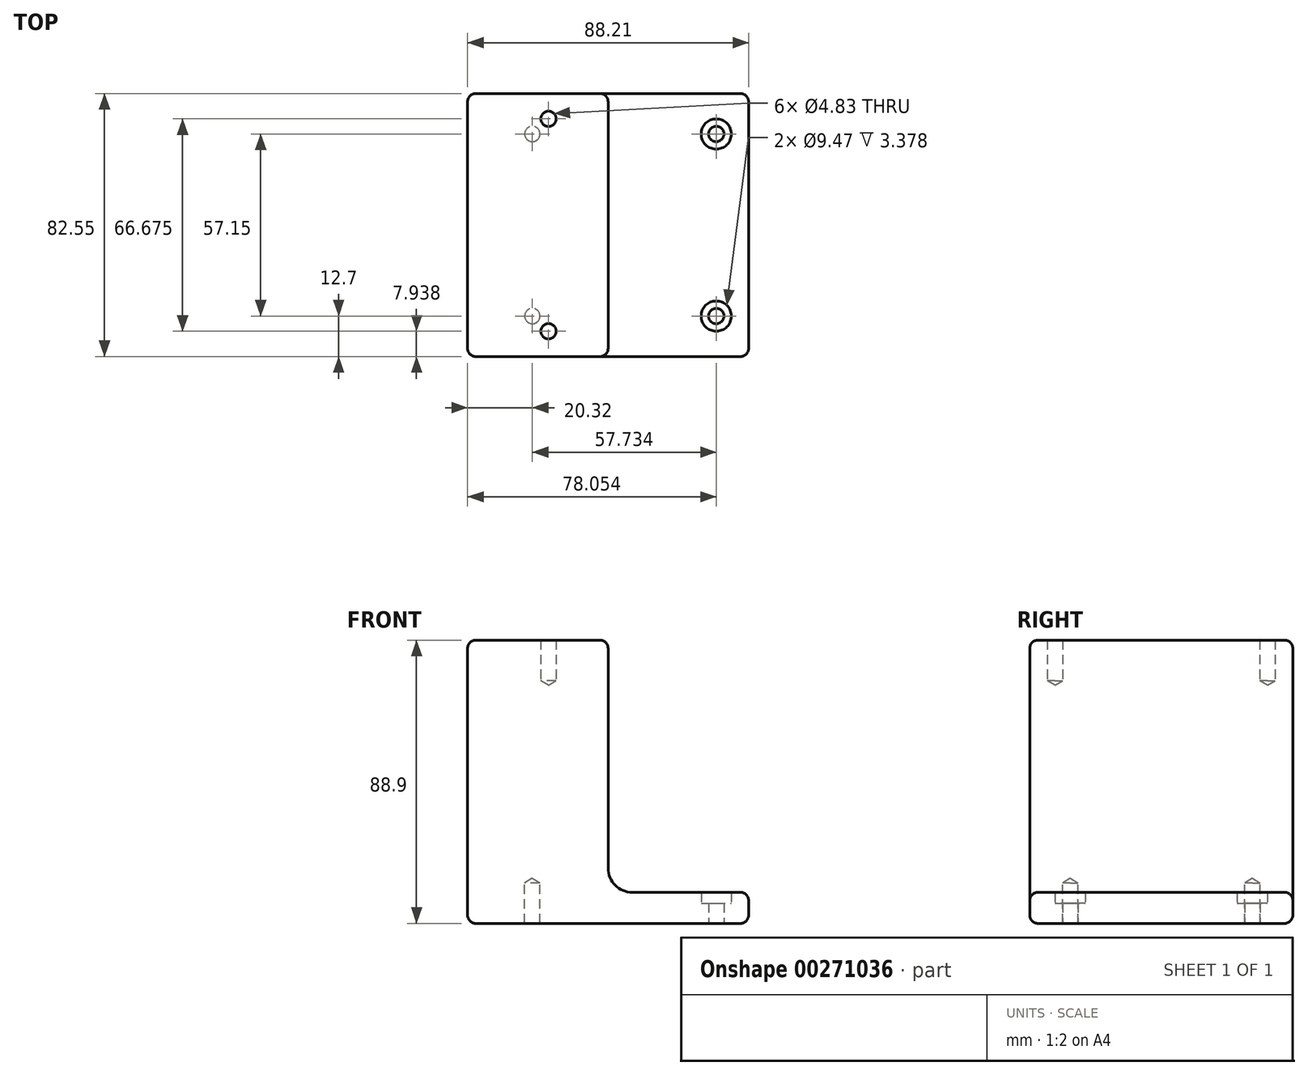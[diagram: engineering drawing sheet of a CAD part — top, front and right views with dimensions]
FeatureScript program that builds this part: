
annotation { "Feature Type Name" : "Feature", "Feature Type Description" : "" }
export const myFeature = defineFeature(function(context is Context, id is Id, definition is map)
    precondition{}
    {
        {
            var Q0;
            Q0=qCreatedBy(makeId("Front.planeOp"),FACE);
            var sketch = newSketch(context, id + "F0", { "sketchPlane" : qUnion([Q0])});
            skLineSegment(sketch, "E0.bottom", {"start": v(0, 0) * mm, "end": v(88.21, 0) * mm});
            skLineSegment(sketch, "E0.top", {"start": v(0, 88.9) * mm, "end": v(44.1, 88.9) * mm});
            skLineSegment(sketch, "E0.left", {"start": v(0, 0) * mm, "end": v(0, 88.9) * mm});
            skLineSegment(sketch, "E0.right", {"start": v(88.21, 0) * mm, "end": v(88.21, 9.73) * mm});
            skLineSegment(sketch, "E1", {"start": v(44.1, 88.9) * mm, "end": v(44.1, 9.73) * mm});
            skPoint(sketch, "E1.endSnap0", {"position": v(44.1, 0) * mm});
            skLineSegment(sketch, "E2", {"start": v(44.1, 9.73) * mm, "end": v(88.21, 9.73) * mm});
            skPoint(sketch, "E3.orphan", {"position": v(88.21, 88.9) * mm});
            skSolve(sketch);
        }
        {
            var Q0;
            Q0 = qSketchRegion(id + "F0", true);
            extrude(context, id + "F1", {"entities" : qUnion([Q0]), "depth" : 82.55 * mm});
        }
        {
            var Q0;
            Q0=makeQuery(id+"F1.opExtrude","SWEPT_EDGE",EDGE,{"disambiguationData":[OSD([sQuery(id+"F0.wireOp",EDGE,"E1"),sQuery(id+"F0.wireOp",EDGE,"E2")])]});
            fillet(context, id + "F2", {"entities" : qUnion([Q0]), "radius" : 7.62 * mm, "tangentPropagation" : true, "allowEdgeOverflow" : false});
        }
        {
            var Q0;
            Q0=makeQuery(id+"F1.opExtrude","SWEPT_EDGE",EDGE,{"disambiguationData":[OSD([sQuery(id+"F0.wireOp",EDGE,"E0.top"),sQuery(id+"F0.wireOp",EDGE,"E1")])]});
            var Q1;
            Q1=makeQuery(id+"F1.opExtrude","SWEPT_EDGE",EDGE,{"disambiguationData":[OSD([sQuery(id+"F0.wireOp",EDGE,"E0.top"),sQuery(id+"F0.wireOp",EDGE,"E0.left")])]});
            var Q2;
            Q2=makeQuery(id+"F1.opExtrude","SWEPT_EDGE",EDGE,{"disambiguationData":[OSD([sQuery(id+"F0.wireOp",EDGE,"E0.bottom"),sQuery(id+"F0.wireOp",EDGE,"E0.left")])]});
            var Q3;
            Q3=makeQuery(id+"F1.opExtrude","SWEPT_EDGE",EDGE,{"disambiguationData":[OSD([sQuery(id+"F0.wireOp",EDGE,"E0.right"),sQuery(id+"F0.wireOp",EDGE,"E2")])]});
            var Q4;
            Q4=makeQuery(id+"F1.opExtrude","SWEPT_EDGE",EDGE,{"disambiguationData":[OSD([sQuery(id+"F0.wireOp",EDGE,"E0.bottom"),sQuery(id+"F0.wireOp",EDGE,"E0.right")])]});
            var Q5;
            Q5=makeQuery(id+"F1.opExtrude","CAP_EDGE",EDGE,{"disambiguationData":[OSD([sQuery(id+"F0.wireOp",EDGE,"E0.top")])],"isStart":true});
            var Q6;
            Q6=makeQuery(id+"F1.opExtrude","CAP_EDGE",EDGE,{"disambiguationData":[OSD([sQuery(id+"F0.wireOp",EDGE,"E0.top")])],"isStart":false});
            var Q7;
            Q7=makeQuery(id+"F1.opExtrude","CAP_EDGE",EDGE,{"disambiguationData":[OSD([sQuery(id+"F0.wireOp",EDGE,"E1")])],"isStart":false});
            var Q8;
            Q8=makeQuery(id+"F1.opExtrude","CAP_EDGE",EDGE,{"disambiguationData":[OSD([sQuery(id+"F0.wireOp",EDGE,"E2")])],"isStart":false});
            var Q9;
            Q9=makeQuery(id+"F1.opExtrude","CAP_EDGE",EDGE,{"disambiguationData":[OSD([sQuery(id+"F0.wireOp",EDGE,"E2")])],"isStart":true});
            var Q10;
            Q10=makeQuery(id+"F1.opExtrude","CAP_EDGE",EDGE,{"disambiguationData":[OSD([sQuery(id+"F0.wireOp",EDGE,"E1")])],"isStart":true});
            var Q11;
            Q11=makeQuery(id+"F1.opExtrude","CAP_EDGE",EDGE,{"disambiguationData":[OSD([sQuery(id+"F0.wireOp",EDGE,"E0.left")])],"isStart":true});
            var Q12;
            Q12=makeQuery(id+"F1.opExtrude","CAP_EDGE",EDGE,{"disambiguationData":[OSD([sQuery(id+"F0.wireOp",EDGE,"E0.bottom")])],"isStart":true});
            var Q13;
            Q13=makeQuery(id+"F1.opExtrude","CAP_EDGE",EDGE,{"disambiguationData":[OSD([sQuery(id+"F0.wireOp",EDGE,"E0.left")])],"isStart":false});
            var Q14;
            Q14=makeQuery(id+"F1.opExtrude","CAP_EDGE",EDGE,{"disambiguationData":[OSD([sQuery(id+"F0.wireOp",EDGE,"E0.bottom")])],"isStart":false});
            var Q15;
            Q15=makeQuery(id+"F1.opExtrude","CAP_EDGE",EDGE,{"disambiguationData":[OSD([sQuery(id+"F0.wireOp",EDGE,"E0.right")])],"isStart":false});
            var Q16;
            Q16=makeQuery(id+"F1.opExtrude","CAP_EDGE",EDGE,{"disambiguationData":[OSD([sQuery(id+"F0.wireOp",EDGE,"E0.right")])],"isStart":true});
            fillet(context, id + "F3", {"entities" : qUnion([Q0, Q1, Q2, Q3, Q4, Q5, Q6, Q7, Q8, Q9, Q10, Q11, Q12, Q13, Q14, Q15, Q16]), "radius" : 2.54 * mm, "tangentPropagation" : true, "allowEdgeOverflow" : false});
        }
        {
            var Q0;
            Q0=makeQuery(id+"F1.opExtrude","SWEPT_FACE",FACE,{"disambiguationData":[OSD([sQuery(id+"F0.wireOp",EDGE,"E0.top")])]});
            var sketch = newSketch(context, id + "F4", { "sketchPlane" : qUnion([Q0])});
            skPoint(sketch, "E4", {"position": v(25.4, -7.94) * mm});
            skPoint(sketch, "E5", {"position": v(25.4, -74.61) * mm});
            skSolve(sketch);
        }
        {
            var Q0;
            Q0=makeQuery(id+"F1.opExtrude","SWEPT_FACE",FACE,{"disambiguationData":[OSD([sQuery(id+"F0.wireOp",EDGE,"E0.bottom")])]});
            var sketch = newSketch(context, id + "F5", { "sketchPlane" : qUnion([Q0])});
            skPoint(sketch, "E6", {"position": v(20.32, 69.85) * mm});
            skPoint(sketch, "E7", {"position": v(20.32, 12.7) * mm});
            skSolve(sketch);
        }
        {
            var Q0;
            Q0=sQuery(id+"F4.wireOp",VERTEX,"E4");
            var Q1;
            Q1=sQuery(id+"F4.wireOp",VERTEX,"E5");
            var Q2;
            Q2=sQuery(id+"F5.wireOp",VERTEX,"E6");
            var Q3;
            Q3=sQuery(id+"F5.wireOp",VERTEX,"E7");
            var Q4;
            Q4=makeQuery(id+"F1.opExtrude","SWEPT_BODY",BODY,{"disambiguationData":[OSD([sQuery(id+"F0.wireOp",EDGE,"E0.bottom"),sQuery(id+"F0.wireOp",EDGE,"E0.top"),sQuery(id+"F0.wireOp",EDGE,"E0.left"),sQuery(id+"F0.wireOp",EDGE,"E0.right"),sQuery(id+"F0.wireOp",EDGE,"E1"),sQuery(id+"F0.wireOp",EDGE,"E2")])]});
            hole(context, id + "F6", {"style" : HoleStyle.SIMPLE, "endStyle" : HoleEndStyle.BLIND, "holeDiameter" : 4.83 * mm, "holeDepth" : 12.7 * mm, "tappedDepth" : 12.7 * mm, "tapClearance" : 3, "locations" : qUnion([Q0, Q1, Q2, Q3]), "scope" : qUnion([Q4])});
        }
        {
            var Q0;
            Q0=makeQuery(id+"F1.opExtrude","SWEPT_FACE",FACE,{"disambiguationData":[OSD([sQuery(id+"F0.wireOp",EDGE,"E2")])]});
            var sketch = newSketch(context, id + "F7", { "sketchPlane" : qUnion([Q0])});
            skPoint(sketch, "E8", {"position": v(78.05, -12.7) * mm});
            skPoint(sketch, "E9", {"position": v(78.05, -69.85) * mm});
            skSolve(sketch);
        }
        {
            var Q0;
            Q0=sQuery(id+"F7.wireOp",VERTEX,"E8");
            var Q1;
            Q1=sQuery(id+"F7.wireOp",VERTEX,"E9");
            var Q2;
            Q2=makeQuery(id+"F1.opExtrude","SWEPT_BODY",BODY,{"disambiguationData":[OSD([sQuery(id+"F0.wireOp",EDGE,"E0.bottom"),sQuery(id+"F0.wireOp",EDGE,"E0.top"),sQuery(id+"F0.wireOp",EDGE,"E0.left"),sQuery(id+"F0.wireOp",EDGE,"E0.right"),sQuery(id+"F0.wireOp",EDGE,"E1"),sQuery(id+"F0.wireOp",EDGE,"E2")])]});
            hole(context, id + "F8", {"style" : HoleStyle.C_BORE, "endStyle" : HoleEndStyle.THROUGH, "holeDiameter" : 4.83 * mm, "cBoreDiameter" : 9.47 * mm, "cBoreDepth" : 3.38 * mm, "tappedDepth" : 12.7 * mm, "tapClearance" : 3, "locations" : qUnion([Q0, Q1]), "scope" : qUnion([Q2])});
        }
    });
